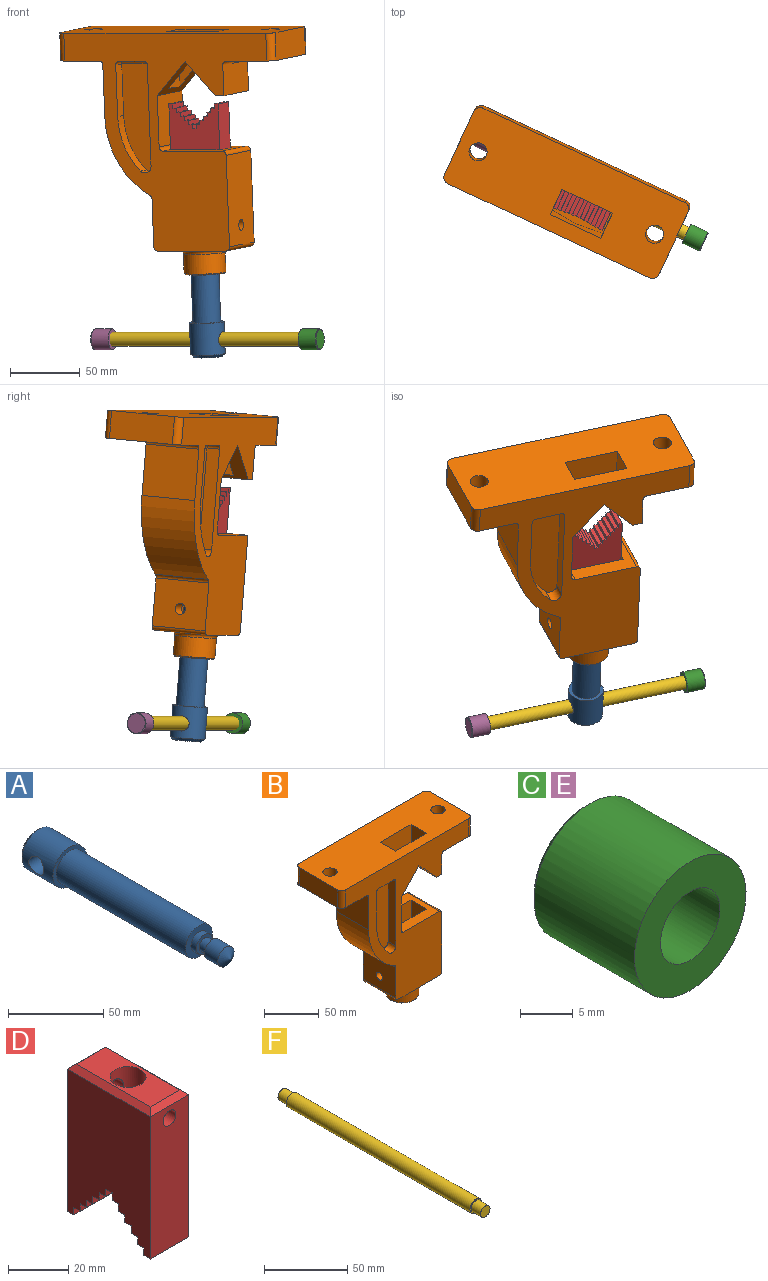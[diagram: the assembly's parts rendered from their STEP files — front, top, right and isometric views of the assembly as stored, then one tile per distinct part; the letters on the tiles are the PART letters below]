
ASSEMBLY  parts=6 mates=6
PART A: 13 faces, bbox 25x144.5x25 mm
  f0: cylinder r=12.5mm len=25mm, axis (0,-1,0), area 1611.6mm2, adj f2,f11,f12
  f1: cylinder r=10mm len=96mm, axis (0,-1,0), area 6031.9mm2, adj f2,f10
  f2: plane 25x25mm, normal (0,-1,0), area 176.7mm2, adj f0,f1
  f3: plane 21x21mm, normal (0,1,0), area 346.4mm2, adj f11
  f4: cone r=0mm half-angle=60deg, axis (0,1,0), area 130.6mm2, adj f5
  f5: cylinder r=6mm len=12mm, axis (0,-1,0), area 377mm2, adj f4,f6
  f6: plane 12x12mm, normal (0,1,0), area 62.8mm2, adj f5,f7
  f7: cylinder r=4mm len=8mm, axis (0,-1,0), area 150.8mm2, adj f6,f8
  f8: plane 12x12mm, normal (0,-1,0), area 62.8mm2, adj f7,f9
  f9: cylinder r=6mm len=12mm, axis (0,-1,0), area 150.8mm2, adj f8,f10
  f10: plane 20x20mm, normal (0,-1,0), area 201.1mm2, adj f1,f9
  f11: cone r=12.5mm half-angle=45deg, axis (0,-1,0), area 204.4mm2, adj f0,f3
  f12: cylinder r=5.5mm len=25mm, axis (-1,0,0), area 820.5mm2, adj f0
PART B: 68 faces, bbox 170x60.8x175 mm
  f0: plane 21x20mm, normal (0,0,1), area 262.9mm2, adj f40,f41,f42,f63
  f1: cylinder r=3mm len=32.79mm, axis (-1,0,0), area 140.8mm2, adj f26,f36,f38,f55
  f2: plane 46.82x42mm, normal (0,0,1), area 1166.3mm2, adj f3,f4,f7,f8,f39,f40,f41,f42
  f3: plane 134x95.03mm, normal (0,1,0), area 6011.2mm2, adj f2,f5,f6,f7,f8,f9,f10,f11
  f4: plane 160x157mm, normal (0,-1,0), area 9795.4mm2, adj f2,f5,f6,f7,f8,f9,f10,f11
  f5: plane 42x37mm, normal (-1,0,0), area 1554mm2, adj f3,f4,f13,f58
  f6: plane 42x37mm, normal (1,0,0), area 1554mm2, adj f3,f4,f7,f14
  f7: cylinder r=3mm len=42mm, axis (0,1,0), area 197.9mm2, adj f2,f3,f4,f6
  f8: cylinder r=3mm len=42mm, axis (0,1,0), area 197.9mm2, adj f2,f3,f4,f9
  f9: plane 66x42mm, normal (1,0,0), area 2721.7mm2, adj f3,f4,f8,f48,f66
  f10: plane 54x42mm, normal (0,0,-1), area 1250.1mm2, adj f3,f4,f64,f65,f66
  f11: plane 42x34.53mm, normal (-1,0,0), area 1400mm2, adj f3,f4,f12,f49,f65
  f12: cylinder r=3mm len=42mm, axis (0,1,0), area 134.1mm2, adj f3,f4,f11,f13
  f13: cylinder r=65mm len=56.85mm, axis (0,1,0), area 2906.2mm2, adj f3,f4,f5,f12
  f14: plane 45x25mm, normal (0.74,0,-0.68), area 863.1mm2, adj f3,f4,f6,f38,f44,f45,f47,f54
  f15: plane 37x10mm, normal (1,0,0), area 370mm2, adj f3,f18,f19,f56
  f16: plane 72.71x10mm, normal (-1,0,0), area 727.1mm2, adj f3,f17,f19,f53
  f17: cylinder r=5mm len=10mm, axis (0,1,0), area 117.3mm2, adj f3,f16,f18,f19
  f18: cylinder r=55mm len=39.28mm, axis (0,1,0), area 437.5mm2, adj f3,f15,f17,f19
  f19: plane 80.71x25mm, normal (0,1,0), area 1782.2mm2, adj f15,f16,f17,f18,f26,f53,f56
  f20: plane 37x10mm, normal (1,0,0), area 370mm2, adj f4,f23,f24,f52
  f21: plane 72.71x10mm, normal (-1,0,0), area 727.1mm2, adj f4,f22,f24,f50
  f22: cylinder r=5mm len=10mm, axis (0,-1,0), area 117.3mm2, adj f4,f21,f23,f24
  f23: cylinder r=55mm len=39.28mm, axis (0,-1,0), area 437.5mm2, adj f4,f20,f22,f24
  f24: plane 77.71x25mm, normal (0,-1,0), area 1711mm2, adj f20,f21,f22,f23,f51
  f25: plane 19x7mm, normal (0,0,-1), area 133mm2, adj f4,f50,f51,f52
  f26: plane 170x60mm, normal (0,0,-1), area 5613.9mm2, adj f1,f4,f19,f27,f28,f29,f30,f31
  f27: plane 50x20mm, normal (-1,0,0), area 1000mm2, adj f26,f28,f33,f34
  f28: cylinder r=5mm len=20mm, axis (0,0,-1), area 157.1mm2, adj f4,f26,f27,f34
  f29: cylinder r=5mm len=20mm, axis (0,0,-1), area 157.1mm2, adj f4,f26,f30,f34
  f30: plane 50x20mm, normal (1,0,0), area 1000mm2, adj f26,f29,f31,f34
  f31: cylinder r=5mm len=20mm, axis (0,0,-1), area 157.1mm2, adj f26,f30,f32,f34
  f32: plane 160x20mm, normal (0,1,0), area 3200mm2, adj f26,f31,f33,f34
  f33: cylinder r=5mm len=20mm, axis (0,0,-1), area 157.1mm2, adj f26,f27,f32,f34
  f34: plane 170x60mm, normal (0,0,1), area 9113.1mm2, adj f4,f27,f28,f29,f30,f31,f32,f33
  f35: plane 42x22mm, normal (1,0,0), area 924mm2, adj f4,f36,f37,f55
  f36: plane 27.06x22mm, normal (0,1,0), area 374.6mm2, adj f1,f35,f37,f38
  f37: plane 42x7mm, normal (0,0,-1), area 294mm2, adj f4,f35,f36,f38
  f38: plane 45x25mm, normal (-0.74,0,-0.67), area 806.2mm2, adj f1,f4,f14,f36,f37,f45,f46,f47
  f39: plane 62x20mm, normal (1,0,0), area 1189.7mm2, adj f2,f40,f42,f43,f49
  f40: plane 62x40mm, normal (0,-1,0), area 2480mm2, adj f0,f2,f39,f41,f43
  f41: plane 62x20mm, normal (-1,0,0), area 1189.7mm2, adj f0,f2,f40,f42,f48
  f42: plane 62x40mm, normal (0,1,0), area 2480mm2, adj f0,f2,f39,f41,f43
  f43: plane 20x19mm, normal (0,0,1), area 222.9mm2, adj f39,f40,f42,f63
  f44: plane 40.86x20mm, normal (1,0,0), area 817.1mm2, adj f14,f34,f45,f47
  f45: plane 42.81x40mm, normal (0,-1,0), area 1237.4mm2, adj f14,f34,f38,f44,f46
  f46: plane 42.81x20mm, normal (-1,0,0), area 856.1mm2, adj f34,f38,f45,f47
  f47: plane 42.81x40mm, normal (0,1,0), area 1237.4mm2, adj f14,f34,f38,f44,f46
  f48: cylinder r=4mm len=9mm, axis (-1,0,0), area 226.2mm2, adj f9,f41
  f49: cylinder r=4mm len=11mm, axis (-1,0,0), area 276.5mm2, adj f11,f39
  f50: cylinder r=3mm len=10mm, axis (0,-1,0), area 42mm2, adj f4,f21,f25,f51
  f51: cylinder r=3mm len=25mm, axis (1,0,0), area 107.5mm2, adj f24,f25,f50,f52
  f52: cylinder r=3mm len=10mm, axis (0,1,0), area 42mm2, adj f4,f20,f25,f51
  f53: cylinder r=3mm len=13mm, axis (0,-1,0), area 52.3mm2, adj f16,f19,f26,f54
  f54: cylinder r=3mm len=33mm, axis (-1,0,0), area 141.8mm2, adj f3,f14,f26,f53
  f55: cylinder r=3mm len=45mm, axis (0,1,0), area 203.1mm2, adj f1,f4,f26,f35
  f56: cylinder r=3mm len=13mm, axis (0,1,0), area 52.3mm2, adj f15,f19,f26,f57
  f57: cylinder r=3mm len=16.23mm, axis (-1,0,0), area 58.5mm2, adj f3,f26,f56,f58
  f58: cylinder r=3mm len=45mm, axis (0,1,0), area 203.1mm2, adj f4,f5,f26,f57
  f59: cylinder r=6.5mm len=20mm, axis (0,0,1), area 816.8mm2, adj f26,f34
  f60: cylinder r=6.5mm len=20mm, axis (0,0,1), area 816.8mm2, adj f26,f34
  f61: cylinder r=15mm len=30mm, axis (0,0,1), area 1338.3mm2, adj f64,f67
  f62: plane 28.4x28.4mm, normal (0,0,-1), area 319.3mm2, adj f63,f67
  f63: cylinder r=10mm len=28mm, axis (0,0,-1), area 1759.3mm2, adj f0,f43,f62
  f64: torus R=18mm, axis (0,0,-1), area 476.4mm2, adj f10,f61
  f65: cylinder r=3mm len=42mm, axis (0,1,0), area 197.9mm2, adj f3,f4,f10,f11
  f66: cylinder r=3mm len=42mm, axis (0,1,0), area 197.9mm2, adj f3,f4,f9,f10
  f67: cone r=14.2mm half-angle=45deg, axis (0,0,1), area 103.8mm2, adj f61,f62
PART C: 6 faces, bbox 15x14x15 mm
  f0: plane 14x14mm, normal (0,1,0), area 153.9mm2, adj f5
  f1: plane 15x15mm, normal (0,-1,0), area 126.4mm2, adj f2,f4
  f2: cylinder r=7.5mm len=15mm, axis (0,-1,0), area 636.2mm2, adj f1,f5
  f3: cone r=4mm half-angle=60deg, axis (0,-1,0), area 58mm2, adj f4
  f4: cylinder r=4mm len=10mm, axis (0,1,0), area 251.3mm2, adj f1,f3
  f5: cone r=7.5mm half-angle=45deg, axis (0,-1,0), area 32.2mm2, adj f0,f2
PART D: 38 faces, bbox 18x39x60 mm
  f0: plane 58x18mm, normal (0,-1,0), area 1015.7mm2, adj f1,f28,f29,f32,f34
  f1: plane 18x3mm, normal (0,0,-1), area 54mm2, adj f0,f2,f28,f29
  f2: plane 18x3mm, normal (0,1,0), area 54mm2, adj f1,f3,f28,f29
  f3: plane 18x3mm, normal (0,0,-1), area 54mm2, adj f2,f4,f28,f29
  f4: plane 18x3mm, normal (0,1,0), area 54mm2, adj f3,f5,f28,f29
  f5: plane 18x3mm, normal (0,0,-1), area 54mm2, adj f4,f6,f28,f29
  f6: plane 18x3mm, normal (0,1,0), area 54mm2, adj f5,f7,f28,f29
  f7: plane 18x3mm, normal (0,0,-1), area 54mm2, adj f6,f8,f28,f29
  f8: plane 18x3mm, normal (0,1,0), area 54mm2, adj f7,f9,f28,f29
  f9: plane 18x3mm, normal (0,0,-1), area 54mm2, adj f8,f10,f28,f29
  f10: plane 18x3mm, normal (0,1,0), area 54mm2, adj f9,f11,f28,f29
  f11: plane 18x3mm, normal (0,0,-1), area 54mm2, adj f10,f12,f28,f29
  f12: plane 18x3mm, normal (0,1,0), area 54mm2, adj f11,f13,f28,f29
  f13: plane 18x3mm, normal (0,0,-1), area 54mm2, adj f12,f14,f28,f29
  f14: plane 18x3mm, normal (0,-1,0), area 54mm2, adj f13,f15,f28,f29
  f15: plane 18x3mm, normal (0,0,-1), area 54mm2, adj f14,f16,f28,f29
  f16: plane 18x3mm, normal (0,-1,0), area 54mm2, adj f15,f17,f28,f29
  f17: plane 18x3mm, normal (0,0,-1), area 54mm2, adj f16,f18,f28,f29
  f18: plane 18x3mm, normal (0,-1,0), area 54mm2, adj f17,f19,f28,f29
  f19: plane 18x3mm, normal (0,0,-1), area 54mm2, adj f18,f20,f28,f29
  f20: plane 18x3mm, normal (0,-1,0), area 54mm2, adj f19,f21,f28,f29
  f21: plane 18x3mm, normal (0,0,-1), area 54mm2, adj f20,f22,f28,f29
  f22: plane 18x3mm, normal (0,-1,0), area 54mm2, adj f21,f23,f28,f29
  f23: plane 18x3mm, normal (0,0,-1), area 54mm2, adj f22,f24,f28,f29
  f24: plane 18x3mm, normal (0,-1,0), area 54mm2, adj f23,f25,f28,f29
  f25: plane 18x3mm, normal (0,0,-1), area 54mm2, adj f24,f26,f28,f29
  f26: plane 58x18mm, normal (0,1,0), area 1015.7mm2, adj f25,f28,f29,f33,f37
  f27: plane 35x14mm, normal (0,0,1), area 376.9mm2, adj f31,f34,f35,f36,f37
  f28: plane 58x39mm, normal (1,0,0), area 1938mm2, adj f0,f1,f2,f3,f4,f5,f6,f7
  f29: plane 58x39mm, normal (-1,0,0), area 1938mm2, adj f0,f1,f2,f3,f4,f5,f6,f7
  f30: cone r=6mm half-angle=60deg, axis (0,0,1), area 130.6mm2, adj f31
  f31: cylinder r=6mm len=20mm, axis (0,0,-1), area 695.5mm2, adj f27,f30,f32,f33
  f32: cylinder r=3mm len=14.3mm, axis (0,-1,0), area 261.9mm2, adj f0,f31
  f33: cylinder r=3mm len=14.3mm, axis (0,-1,0), area 261.9mm2, adj f26,f31
  f34: plane 18x2mm, normal (0,-0.71,0.71), area 45.3mm2, adj f0,f27,f35,f36
  f35: plane 39x2mm, normal (0.71,0,0.71), area 104.7mm2, adj f27,f28,f34,f37
  f36: plane 39x2mm, normal (-0.71,0,0.71), area 104.7mm2, adj f27,f29,f34,f37
  f37: plane 18x2mm, normal (0,0.71,0.71), area 45.3mm2, adj f26,f27,f35,f36
PART E: same geometry as C
PART F: 7 faces, bbox 10x172x10 mm
  f0: plane 8x8mm, normal (0,1,0), area 50.3mm2, adj f1
  f1: cylinder r=4mm len=8mm, axis (0,-1,0), area 201.1mm2, adj f0,f2
  f2: plane 10x10mm, normal (0,1,0), area 28.3mm2, adj f1,f3
  f3: cylinder r=5mm len=156mm, axis (0,-1,0), area 4900.9mm2, adj f2,f4
  f4: plane 10x10mm, normal (0,-1,0), area 28.3mm2, adj f3,f5
  f5: cylinder r=4mm len=8mm, axis (0,-1,0), area 201.1mm2, adj f4,f6
  f6: plane 8x8mm, normal (0,-1,0), area 50.3mm2, adj f5
PLACE A rot(axis=(-0.16,-0.73,0.67),163.2deg) t=(95.88,-39.53,-197.85)mm
PLACE B rot(axis=(0.19,-0.04,-0.98),25.5deg) t=(-11.53,-33.2,14.51)mm
PLACE C rot(axis=(0.04,0.03,-1),115.1deg) t=(176.31,-78.23,-185.39)mm
PLACE D rot(axis=(-0.84,-0.54,-0.04),177.3deg) t=(67.68,-53.87,-16.33)mm
PLACE E rot(axis=(0.04,-0.07,1),65.2deg) t=(14.54,-2.8,-185.39)mm
PLACE F rot(axis=(0.04,-0.07,1),65.2deg) t=(17.48,-4.17,-185.39)mm
MATE slider F.f1 <-> A.f12  axis (0.91,-0.42,0) through (95.42,-40.51,-185.39)mm
MATE fastened D.f30 <-> A.f0  axis (-0.04,-0.08,1) through (91.35,-49.24,-75.31)mm
MATE planar B.f61 <-> A.f0  axis (0.04,0.08,-1) through (93.67,-44.27,-138.07)mm
MATE fastened C.f2 <-> F.f1  axis (-0.91,0.42,0) through (169.74,-75.17,-185.39)mm
MATE slider A.f0 <-> B.f61  axis (-0.04,-0.08,1) through (91.43,-49.08,-77.31)mm
MATE fastened E.f2 <-> F.f1  axis (0.91,-0.42,0) through (21.11,-5.86,-185.39)mm
